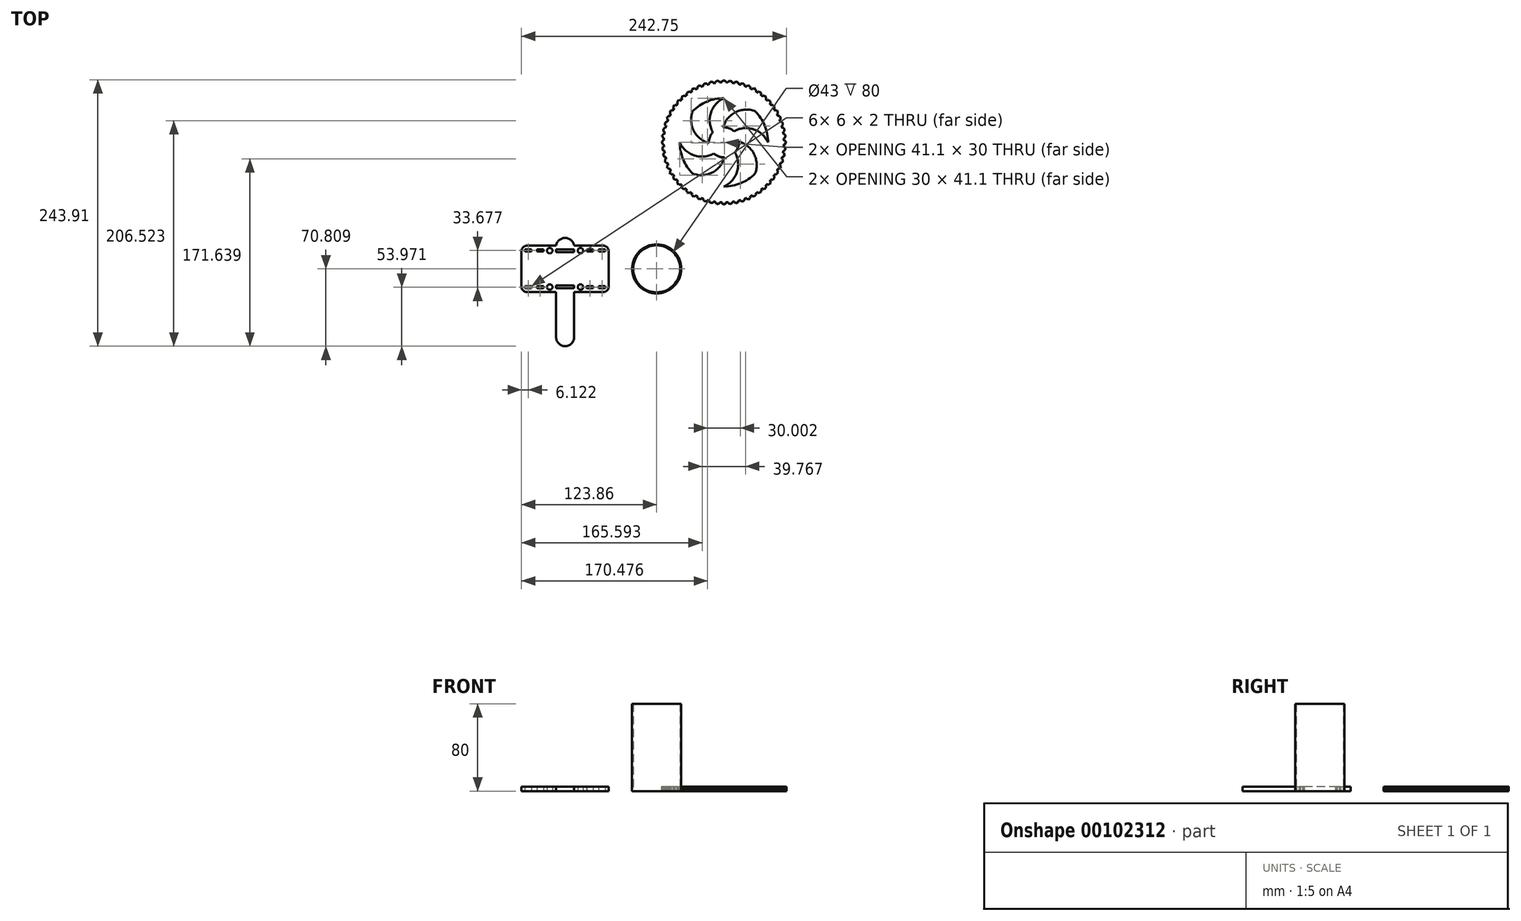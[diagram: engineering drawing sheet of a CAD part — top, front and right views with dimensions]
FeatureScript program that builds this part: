
annotation { "Feature Type Name" : "Feature", "Feature Type Description" : "" }
export const myFeature = defineFeature(function(context is Context, id is Id, definition is map)
    precondition{}
    {
        {
            var Q0;
            Q0=qCreatedBy(makeId("Top.planeOp"),FACE);
            var sketch = newSketch(context, id + "F0", { "sketchPlane" : qUnion([Q0])});
            skCircle(sketch, "E0", {"center": v(105.48, 9.3) * mm, "radius": 55 * mm});
            skLineSegment(sketch, "E1.bottom", {"start": v(-5, -85.33) * mm, "end": v(-31.7, -85.33) * mm});
            skLineSegment(sketch, "E1.top", {"start": v(-5, -127.71) * mm, "end": v(-31.7, -127.71) * mm});
            skLineSegment(sketch, "E1.left", {"start": v(0, -90.33) * mm, "end": v(0, -122.71) * mm});
            skLineSegment(sketch, "E1.right", {"start": v(-80, -90.33) * mm, "end": v(-80, -122.71) * mm});
            skArc(sketch, "E2", {"start": v(65.04, 9.3) * mm, "mid": v(68.12, -6.16) * mm, "end": v(76.89, -19.28) * mm});
            skArc(sketch, "E3", {"start": v(115.62, 0.11) * mm, "mid": v(118.37, 4.7) * mm, "end": v(119.15, 9.98) * mm});
            skArc(sketch, "E4", {"start": v(105.48, 49.74) * mm, "mid": v(93.48, 36.37) * mm, "end": v(95.33, 18.5) * mm});
            skArc(sketch, "E5.1.0", {"start": v(76.89, 37.9) * mm, "mid": v(77.86, 19.97) * mm, "end": v(91.8, 8.64) * mm});
            skArc(sketch, "E5.2.0", {"start": v(65.04, 9.3) * mm, "mid": v(78.41, -2.68) * mm, "end": v(96.28, -0.83) * mm});
            skArc(sketch, "E5.3.0", {"start": v(76.89, -19.28) * mm, "mid": v(94.82, -18.3) * mm, "end": v(106.14, -4.37) * mm});
            skArc(sketch, "E5.4.0", {"start": v(105.48, -31.13) * mm, "mid": v(117.47, -17.75) * mm, "end": v(115.62, 0.11) * mm});
            skArc(sketch, "E5.5.0", {"start": v(134.07, -19.28) * mm, "mid": v(133.1, -1.35) * mm, "end": v(119.15, 9.98) * mm});
            skArc(sketch, "E5.6.0", {"start": v(145.91, 9.3) * mm, "mid": v(132.54, 21.3) * mm, "end": v(114.68, 19.45) * mm});
            skArc(sketch, "E5.7.0", {"start": v(134.07, 37.9) * mm, "mid": v(116.13, 36.93) * mm, "end": v(104.8, 22.99) * mm});
            skArc(sketch, "E6.trimOffspring", {"start": v(95.33, 18.5) * mm, "mid": v(92.59, 13.93) * mm, "end": v(91.8, 8.64) * mm});
            skArc(sketch, "E7.trimOffspring", {"start": v(96.28, -0.83) * mm, "mid": v(100.86, -3.58) * mm, "end": v(106.14, -4.37) * mm});
            skArc(sketch, "E8.trimOffspring", {"start": v(105.48, -31.13) * mm, "mid": v(120.95, -28.05) * mm, "end": v(134.07, -19.28) * mm});
            skArc(sketch, "E9.trimOffspring", {"start": v(145.91, 9.3) * mm, "mid": v(142.83, 24.78) * mm, "end": v(134.07, 37.9) * mm});
            skArc(sketch, "E10.trimOffspring", {"start": v(105.48, 49.74) * mm, "mid": v(90, 46.67) * mm, "end": v(76.89, 37.9) * mm});
            skArc(sketch, "E11.trimOffspring", {"start": v(114.68, 19.45) * mm, "mid": v(110.1, 22.2) * mm, "end": v(104.8, 22.99) * mm});
            skLineSegment(sketch, "E12.bottom", {"start": v(-76.88, -124.36) * mm, "end": v(-70.88, -124.36) * mm});
            skLineSegment(sketch, "E12.top", {"start": v(-76.88, -122.36) * mm, "end": v(-70.88, -122.36) * mm});
            skLineSegment(sketch, "E12.left", {"start": v(-76.88, -124.36) * mm, "end": v(-76.88, -122.36) * mm});
            skLineSegment(sketch, "E12.right", {"start": v(-70.88, -124.36) * mm, "end": v(-70.88, -122.36) * mm});
            skLineSegment(sketch, "E13.bottom", {"start": v(-65.79, -124.36) * mm, "end": v(-59.79, -124.36) * mm});
            skLineSegment(sketch, "E13.top", {"start": v(-65.79, -122.36) * mm, "end": v(-59.79, -122.36) * mm});
            skLineSegment(sketch, "E13.left", {"start": v(-65.79, -124.36) * mm, "end": v(-65.79, -122.36) * mm});
            skLineSegment(sketch, "E13.right", {"start": v(-59.79, -124.36) * mm, "end": v(-59.79, -122.36) * mm});
            skLineSegment(sketch, "E14.MirrorCS", {"start": v(-76.88, -88.68) * mm, "end": v(-70.88, -88.68) * mm});
            skLineSegment(sketch, "E15.MirrorCS", {"start": v(-76.88, -88.68) * mm, "end": v(-76.88, -90.68) * mm});
            skLineSegment(sketch, "E16.MirrorCS", {"start": v(-70.88, -88.68) * mm, "end": v(-70.88, -90.68) * mm});
            skLineSegment(sketch, "E17.MirrorCS", {"start": v(-65.79, -88.68) * mm, "end": v(-65.79, -90.68) * mm});
            skLineSegment(sketch, "E18.MirrorCS", {"start": v(-65.79, -88.68) * mm, "end": v(-59.79, -88.68) * mm});
            skLineSegment(sketch, "E19.MirrorCS", {"start": v(-65.79, -90.68) * mm, "end": v(-59.79, -90.68) * mm});
            skLineSegment(sketch, "E20.MirrorCS", {"start": v(-59.87, -88.68) * mm, "end": v(-59.87, -90.68) * mm});
            skLineSegment(sketch, "E21", {"start": v(-76.88, -90.68) * mm, "end": v(-70.88, -90.68) * mm});
            skPoint(sketch, "E22.visualSharp", {"position": v(-80, -127.71) * mm});
            skArc(sketch, "E22.filletArc", {"start": v(-80, -122.71) * mm, "mid": v(-78.54, -126.25) * mm, "end": v(-75, -127.71) * mm});
            skPoint(sketch, "E23.visualSharp", {"position": v(0, -85.33) * mm});
            skArc(sketch, "E23.filletArc", {"start": v(0, -90.33) * mm, "mid": v(-1.46, -86.8) * mm, "end": v(-5, -85.33) * mm});
            skPoint(sketch, "E24.visualSharp", {"position": v(-80, -85.33) * mm});
            skArc(sketch, "E24.filletArc", {"start": v(-75, -85.33) * mm, "mid": v(-78.54, -86.8) * mm, "end": v(-80, -90.33) * mm});
            skLineSegment(sketch, "E25", {"start": v(-40, -127.71) * mm, "end": v(-40, -85.33) * mm, "construction": true});
            skLineSegment(sketch, "E26.MirrorCS", {"start": v(-14.21, -124.36) * mm, "end": v(-14.21, -122.36) * mm});
            skLineSegment(sketch, "E27.MirrorCS", {"start": v(-9.12, -124.36) * mm, "end": v(-9.12, -122.36) * mm});
            skLineSegment(sketch, "E28.MirrorCS", {"start": v(-9.12, -88.68) * mm, "end": v(-9.12, -90.68) * mm});
            skLineSegment(sketch, "E29.MirrorCS", {"start": v(-3.12, -88.68) * mm, "end": v(-3.12, -90.68) * mm});
            skLineSegment(sketch, "E30.MirrorCS", {"start": v(-3.12, -88.68) * mm, "end": v(-9.12, -88.68) * mm});
            skLineSegment(sketch, "E31.MirrorCS", {"start": v(-20.13, -88.68) * mm, "end": v(-20.13, -90.68) * mm});
            skLineSegment(sketch, "E32.MirrorCS", {"start": v(-14.21, -88.68) * mm, "end": v(-14.21, -90.68) * mm});
            skLineSegment(sketch, "E33.MirrorCS", {"start": v(-3.12, -124.36) * mm, "end": v(-9.12, -124.36) * mm});
            skLineSegment(sketch, "E34.MirrorCS", {"start": v(-3.12, -124.36) * mm, "end": v(-3.12, -122.36) * mm});
            skLineSegment(sketch, "E35.MirrorCS", {"start": v(-20.21, -124.36) * mm, "end": v(-20.21, -122.36) * mm});
            skLineSegment(sketch, "E36.MirrorCS", {"start": v(-3.12, -122.36) * mm, "end": v(-9.12, -122.36) * mm});
            skLineSegment(sketch, "E37.MirrorCS", {"start": v(-3.12, -90.68) * mm, "end": v(-9.12, -90.68) * mm});
            skPoint(sketch, "E38.MirrorP", {"position": v(0, -127.71) * mm});
            skLineSegment(sketch, "E39.MirrorCS", {"start": v(-14.21, -122.36) * mm, "end": v(-20.21, -122.36) * mm});
            skLineSegment(sketch, "E40.MirrorCS", {"start": v(-14.21, -124.36) * mm, "end": v(-20.21, -124.36) * mm});
            skLineSegment(sketch, "E41.MirrorCS", {"start": v(-14.21, -90.68) * mm, "end": v(-20.21, -90.68) * mm});
            skLineSegment(sketch, "E42.MirrorCS", {"start": v(-14.21, -88.68) * mm, "end": v(-20.21, -88.68) * mm});
            skArc(sketch, "E43.MirrorCS", {"start": v(0, -122.71) * mm, "mid": v(-1.46, -126.25) * mm, "end": v(-5, -127.71) * mm});
            skLineSegment(sketch, "E44.bottom", {"start": v(-48.3, -124.25) * mm, "end": v(-31.7, -124.25) * mm});
            skLineSegment(sketch, "E44.top", {"start": v(-48.3, -121.77) * mm, "end": v(-31.7, -121.77) * mm});
            skLineSegment(sketch, "E44.left", {"start": v(-48.3, -124.25) * mm, "end": v(-48.3, -121.77) * mm});
            skLineSegment(sketch, "E44.right", {"start": v(-31.7, -124.25) * mm, "end": v(-31.7, -121.77) * mm});
            skPoint(sketch, "E44.middle", {"position": v(-40, -123) * mm});
            skLineSegment(sketch, "E45", {"start": v(-40, -106.52) * mm, "end": v(-20.74, -106.52) * mm, "construction": true});
            skLineSegment(sketch, "E46.MirrorCS", {"start": v(-48.3, -91.28) * mm, "end": v(-31.7, -91.28) * mm});
            skLineSegment(sketch, "E47.MirrorCS", {"start": v(-48.3, -88.79) * mm, "end": v(-48.3, -91.28) * mm});
            skLineSegment(sketch, "E48.MirrorCS", {"start": v(-48.3, -88.79) * mm, "end": v(-31.7, -88.79) * mm});
            skLineSegment(sketch, "E49.MirrorCS", {"start": v(-31.7, -88.79) * mm, "end": v(-31.7, -91.28) * mm});
            skLineSegment(sketch, "E50", {"start": v(-59.87, -89.68) * mm, "end": v(-48.3, -90.03) * mm, "construction": true});
            skCircle(sketch, "E51", {"center": v(-54.09, -89.86) * mm, "radius": 2.5 * mm});
            skCircle(sketch, "E52.MirrorC", {"center": v(-25.91, -89.86) * mm, "radius": 2.5 * mm});
            skCircle(sketch, "E53.MirrorC", {"center": v(-25.91, -123.18) * mm, "radius": 2.5 * mm});
            skCircle(sketch, "E54.MirrorC", {"center": v(-54.09, -123.18) * mm, "radius": 2.5 * mm});
            skCircle(sketch, "E55", {"center": v(43.86, -106.52) * mm, "radius": 21.5 * mm});
            skPoint(sketch, "E55.centerSnap0", {"position": v(0, -106.52) * mm});
            skCircle(sketch, "E56.0", {"center": v(43.86, -106.52) * mm, "radius": 22.5 * mm});
            skArc(sketch, "E57.MirrorCS", {"start": v(-48.3, -85.33) * mm, "mid": v(-40, -78.22) * mm, "end": v(-31.7, -85.33) * mm});
            skLineSegment(sketch, "E58", {"start": v(-48.3, -127.71) * mm, "end": v(-48.3, -169.03) * mm});
            skLineSegment(sketch, "E59", {"start": v(-31.7, -127.71) * mm, "end": v(-31.7, -169.03) * mm});
            skArc(sketch, "E60", {"start": v(-48.3, -169.03) * mm, "mid": v(-40, -177.33) * mm, "end": v(-31.7, -169.03) * mm});
            skLineSegment(sketch, "E61.trimOffspring", {"start": v(-48.3, -127.71) * mm, "end": v(-75, -127.71) * mm});
            skLineSegment(sketch, "E62.trimOffspring", {"start": v(-48.3, -85.33) * mm, "end": v(-75, -85.33) * mm});
            skLineSegment(sketch, "E63", {"start": v(105.48, 9.3) * mm, "end": v(105.48, -47.96) * mm, "construction": true});
            skArc(sketch, "E64", {"start": v(106.51, -47) * mm, "mid": v(105.78, -47.26) * mm, "end": v(105.48, -47.96) * mm});
            skArc(sketch, "E65", {"start": v(106.51, -47) * mm, "mid": v(107.3, -46.57) * mm, "end": v(107.26, -45.66) * mm});
            skArc(sketch, "E66.MirrorCS", {"start": v(104.44, -47) * mm, "mid": v(103.65, -46.57) * mm, "end": v(103.7, -45.66) * mm});
            skArc(sketch, "E67.MirrorCS", {"start": v(104.44, -47) * mm, "mid": v(105.17, -47.26) * mm, "end": v(105.48, -47.96) * mm});
            skArc(sketch, "E68.1.0", {"start": v(112.4, -46.59) * mm, "mid": v(111.7, -46.91) * mm, "end": v(111.46, -47.65) * mm});
            skArc(sketch, "E68.1.1", {"start": v(110.33, -46.8) * mm, "mid": v(109.5, -46.45) * mm, "end": v(109.45, -45.55) * mm});
            skArc(sketch, "E68.1.2", {"start": v(110.33, -46.8) * mm, "mid": v(111.08, -46.98) * mm, "end": v(111.46, -47.65) * mm});
            skArc(sketch, "E68.1.3", {"start": v(112.4, -46.59) * mm, "mid": v(113.14, -46.07) * mm, "end": v(113, -45.17) * mm});
            skArc(sketch, "E68.2.0", {"start": v(118.2, -45.56) * mm, "mid": v(117.54, -45.96) * mm, "end": v(117.38, -46.71) * mm});
            skArc(sketch, "E68.2.1", {"start": v(116.17, -45.99) * mm, "mid": v(115.3, -45.73) * mm, "end": v(115.17, -44.83) * mm});
            skArc(sketch, "E68.2.2", {"start": v(116.17, -45.99) * mm, "mid": v(116.94, -46.08) * mm, "end": v(117.38, -46.71) * mm});
            skArc(sketch, "E68.2.3", {"start": v(118.2, -45.56) * mm, "mid": v(118.89, -44.97) * mm, "end": v(118.65, -44.1) * mm});
            skArc(sketch, "E68.3.0", {"start": v(123.86, -43.93) * mm, "mid": v(123.25, -44.4) * mm, "end": v(123.17, -45.16) * mm});
            skArc(sketch, "E68.3.1", {"start": v(121.9, -44.57) * mm, "mid": v(121, -44.4) * mm, "end": v(120.77, -43.52) * mm});
            skArc(sketch, "E68.3.2", {"start": v(121.9, -44.57) * mm, "mid": v(122.66, -44.58) * mm, "end": v(123.17, -45.16) * mm});
            skArc(sketch, "E68.3.3", {"start": v(123.86, -43.93) * mm, "mid": v(124.49, -43.27) * mm, "end": v(124.16, -42.42) * mm});
            skArc(sketch, "E68.4.0", {"start": v(129.33, -41.71) * mm, "mid": v(128.77, -42.24) * mm, "end": v(128.77, -43.01) * mm});
            skArc(sketch, "E68.4.1", {"start": v(127.44, -42.56) * mm, "mid": v(126.53, -42.48) * mm, "end": v(126.2, -41.63) * mm});
            skArc(sketch, "E68.4.2", {"start": v(127.44, -42.56) * mm, "mid": v(128.2, -42.5) * mm, "end": v(128.77, -43.01) * mm});
            skArc(sketch, "E68.4.3", {"start": v(129.33, -41.71) * mm, "mid": v(129.88, -41) * mm, "end": v(129.46, -40.19) * mm});
            skArc(sketch, "E68.5.0", {"start": v(134.53, -38.94) * mm, "mid": v(134.03, -39.52) * mm, "end": v(134.11, -40.29) * mm});
            skArc(sketch, "E68.5.1", {"start": v(132.74, -39.98) * mm, "mid": v(131.83, -40) * mm, "end": v(131.42, -39.19) * mm});
            skArc(sketch, "E68.5.2", {"start": v(132.74, -39.98) * mm, "mid": v(133.5, -39.83) * mm, "end": v(134.11, -40.29) * mm});
            skArc(sketch, "E68.5.3", {"start": v(134.53, -38.94) * mm, "mid": v(135, -38.17) * mm, "end": v(134.5, -37.4) * mm});
            skArc(sketch, "E68.6.0", {"start": v(139.41, -35.64) * mm, "mid": v(138.97, -36.27) * mm, "end": v(139.14, -37.02) * mm});
            skArc(sketch, "E68.6.1", {"start": v(137.74, -36.86) * mm, "mid": v(136.84, -36.97) * mm, "end": v(136.35, -36.2) * mm});
            skArc(sketch, "E68.6.2", {"start": v(137.74, -36.86) * mm, "mid": v(138.48, -36.63) * mm, "end": v(139.14, -37.02) * mm});
            skArc(sketch, "E68.6.3", {"start": v(139.41, -35.64) * mm, "mid": v(139.8, -34.82) * mm, "end": v(139.23, -34.12) * mm});
            skArc(sketch, "E68.7.0", {"start": v(143.93, -31.85) * mm, "mid": v(143.56, -32.52) * mm, "end": v(143.8, -33.25) * mm});
            skArc(sketch, "E68.7.1", {"start": v(142.39, -33.23) * mm, "mid": v(141.5, -33.44) * mm, "end": v(140.94, -32.73) * mm});
            skArc(sketch, "E68.7.2", {"start": v(142.39, -33.23) * mm, "mid": v(143.1, -32.93) * mm, "end": v(143.8, -33.25) * mm});
            skArc(sketch, "E68.7.3", {"start": v(143.93, -31.85) * mm, "mid": v(144.23, -30.99) * mm, "end": v(143.58, -30.35) * mm});
            skArc(sketch, "E68.8.0", {"start": v(148.02, -27.6) * mm, "mid": v(147.72, -28.31) * mm, "end": v(148.04, -29.01) * mm});
            skArc(sketch, "E68.8.1", {"start": v(146.63, -29.14) * mm, "mid": v(145.78, -29.44) * mm, "end": v(145.14, -28.8) * mm});
            skArc(sketch, "E68.8.2", {"start": v(146.63, -29.14) * mm, "mid": v(147.3, -28.77) * mm, "end": v(148.04, -29.01) * mm});
            skArc(sketch, "E68.8.3", {"start": v(148.02, -27.6) * mm, "mid": v(148.23, -26.72) * mm, "end": v(147.52, -26.15) * mm});
            skArc(sketch, "E68.9.0", {"start": v(151.64, -22.95) * mm, "mid": v(151.42, -23.69) * mm, "end": v(151.81, -24.35) * mm});
            skArc(sketch, "E68.9.1", {"start": v(150.43, -24.63) * mm, "mid": v(149.6, -25.02) * mm, "end": v(148.9, -24.44) * mm});
            skArc(sketch, "E68.9.2", {"start": v(150.43, -24.63) * mm, "mid": v(151.06, -24.19) * mm, "end": v(151.81, -24.35) * mm});
            skArc(sketch, "E68.9.3", {"start": v(151.64, -22.95) * mm, "mid": v(151.76, -22.05) * mm, "end": v(151, -21.56) * mm});
            skArc(sketch, "E68.10.0", {"start": v(154.76, -17.95) * mm, "mid": v(154.62, -18.7) * mm, "end": v(155.08, -19.33) * mm});
            skArc(sketch, "E68.10.1", {"start": v(153.73, -19.74) * mm, "mid": v(152.95, -20.22) * mm, "end": v(152.2, -19.72) * mm});
            skArc(sketch, "E68.10.2", {"start": v(153.73, -19.74) * mm, "mid": v(154.31, -19.24) * mm, "end": v(155.08, -19.33) * mm});
            skArc(sketch, "E68.10.3", {"start": v(154.76, -17.95) * mm, "mid": v(154.78, -17.04) * mm, "end": v(153.97, -16.64) * mm});
            skArc(sketch, "E68.11.0", {"start": v(157.34, -12.65) * mm, "mid": v(157.28, -13.42) * mm, "end": v(157.8, -13.98) * mm});
            skArc(sketch, "E68.11.1", {"start": v(156.5, -14.54) * mm, "mid": v(155.78, -15.1) * mm, "end": v(154.97, -14.67) * mm});
            skArc(sketch, "E68.11.2", {"start": v(156.5, -14.54) * mm, "mid": v(157.03, -13.98) * mm, "end": v(157.8, -13.98) * mm});
            skArc(sketch, "E68.11.3", {"start": v(157.34, -12.65) * mm, "mid": v(157.27, -11.74) * mm, "end": v(156.42, -11.42) * mm});
            skArc(sketch, "E68.12.0", {"start": v(159.35, -7.1) * mm, "mid": v(159.37, -7.88) * mm, "end": v(159.95, -8.39) * mm});
            skArc(sketch, "E68.12.1", {"start": v(158.71, -9.08) * mm, "mid": v(158.05, -9.7) * mm, "end": v(157.2, -9.37) * mm});
            skArc(sketch, "E68.12.2", {"start": v(158.71, -9.08) * mm, "mid": v(159.18, -8.46) * mm, "end": v(159.95, -8.39) * mm});
            skArc(sketch, "E68.12.3", {"start": v(159.35, -7.1) * mm, "mid": v(159.18, -6.22) * mm, "end": v(158.3, -5.99) * mm});
            skArc(sketch, "E68.13.0", {"start": v(160.77, -1.39) * mm, "mid": v(160.87, -2.15) * mm, "end": v(161.5, -2.6) * mm});
            skArc(sketch, "E68.13.1", {"start": v(160.34, -3.41) * mm, "mid": v(159.75, -4.1) * mm, "end": v(158.88, -3.86) * mm});
            skArc(sketch, "E68.13.2", {"start": v(160.34, -3.41) * mm, "mid": v(160.74, -2.75) * mm, "end": v(161.5, -2.6) * mm});
            skArc(sketch, "E68.13.3", {"start": v(160.77, -1.39) * mm, "mid": v(160.51, -0.52) * mm, "end": v(159.62, -0.38) * mm});
            skArc(sketch, "E68.14.0", {"start": v(161.59, 4.45) * mm, "mid": v(161.76, 3.7) * mm, "end": v(162.43, 3.32) * mm});
            skArc(sketch, "E68.14.1", {"start": v(161.37, 2.4) * mm, "mid": v(160.86, 1.65) * mm, "end": v(159.96, 1.8) * mm});
            skArc(sketch, "E68.14.2", {"start": v(161.37, 2.4) * mm, "mid": v(161.7, 3.1) * mm, "end": v(162.43, 3.32) * mm});
            skArc(sketch, "E68.14.3", {"start": v(161.59, 4.45) * mm, "mid": v(161.24, 5.3) * mm, "end": v(160.33, 5.33) * mm});
            skArc(sketch, "E68.15.0", {"start": v(161.79, 10.34) * mm, "mid": v(162.04, 9.62) * mm, "end": v(162.75, 9.3) * mm});
            skArc(sketch, "E68.15.1", {"start": v(161.79, 8.27) * mm, "mid": v(161.35, 7.48) * mm, "end": v(160.45, 7.53) * mm});
            skArc(sketch, "E68.15.2", {"start": v(161.79, 8.27) * mm, "mid": v(162.04, 9) * mm, "end": v(162.75, 9.3) * mm});
            skArc(sketch, "E68.15.3", {"start": v(161.79, 10.34) * mm, "mid": v(161.35, 11.14) * mm, "end": v(160.45, 11.09) * mm});
            skArc(sketch, "E68.16.0", {"start": v(161.37, 16.23) * mm, "mid": v(161.7, 15.53) * mm, "end": v(162.43, 15.3) * mm});
            skArc(sketch, "E68.16.1", {"start": v(161.59, 14.17) * mm, "mid": v(161.24, 13.33) * mm, "end": v(160.33, 13.29) * mm});
            skArc(sketch, "E68.16.2", {"start": v(161.59, 14.17) * mm, "mid": v(161.76, 14.92) * mm, "end": v(162.43, 15.3) * mm});
            skArc(sketch, "E68.16.3", {"start": v(161.37, 16.23) * mm, "mid": v(160.86, 16.97) * mm, "end": v(159.96, 16.83) * mm});
            skArc(sketch, "E68.17.0", {"start": v(160.34, 22.03) * mm, "mid": v(160.74, 21.37) * mm, "end": v(161.5, 21.22) * mm});
            skArc(sketch, "E68.17.1", {"start": v(160.77, 20) * mm, "mid": v(160.51, 19.14) * mm, "end": v(159.62, 19) * mm});
            skArc(sketch, "E68.17.2", {"start": v(160.77, 20) * mm, "mid": v(160.87, 20.77) * mm, "end": v(161.5, 21.22) * mm});
            skArc(sketch, "E68.17.3", {"start": v(160.34, 22.03) * mm, "mid": v(159.75, 22.72) * mm, "end": v(158.88, 22.48) * mm});
            skArc(sketch, "E68.18.0", {"start": v(158.71, 27.7) * mm, "mid": v(159.18, 27.08) * mm, "end": v(159.95, 27) * mm});
            skArc(sketch, "E68.18.1", {"start": v(159.35, 25.73) * mm, "mid": v(159.18, 24.83) * mm, "end": v(158.3, 24.6) * mm});
            skArc(sketch, "E68.18.2", {"start": v(159.35, 25.73) * mm, "mid": v(159.37, 26.5) * mm, "end": v(159.95, 27) * mm});
            skArc(sketch, "E68.18.3", {"start": v(158.71, 27.7) * mm, "mid": v(158.05, 28.32) * mm, "end": v(157.2, 27.99) * mm});
            skArc(sketch, "E68.19.0", {"start": v(156.5, 33.16) * mm, "mid": v(157.03, 32.6) * mm, "end": v(157.8, 32.6) * mm});
            skArc(sketch, "E68.19.1", {"start": v(157.34, 31.27) * mm, "mid": v(157.27, 30.36) * mm, "end": v(156.42, 30.04) * mm});
            skArc(sketch, "E68.19.2", {"start": v(157.34, 31.27) * mm, "mid": v(157.28, 32.04) * mm, "end": v(157.8, 32.6) * mm});
            skArc(sketch, "E68.19.3", {"start": v(156.5, 33.16) * mm, "mid": v(155.78, 33.7) * mm, "end": v(154.97, 33.3) * mm});
            skArc(sketch, "E68.20.0", {"start": v(153.73, 38.36) * mm, "mid": v(154.31, 37.86) * mm, "end": v(155.08, 37.95) * mm});
            skArc(sketch, "E68.20.1", {"start": v(154.76, 36.57) * mm, "mid": v(154.78, 35.66) * mm, "end": v(153.97, 35.25) * mm});
            skArc(sketch, "E68.20.2", {"start": v(154.76, 36.57) * mm, "mid": v(154.62, 37.33) * mm, "end": v(155.08, 37.95) * mm});
            skArc(sketch, "E68.20.3", {"start": v(153.73, 38.36) * mm, "mid": v(152.95, 38.83) * mm, "end": v(152.2, 38.34) * mm});
            skArc(sketch, "E68.21.0", {"start": v(150.43, 43.25) * mm, "mid": v(151.06, 42.8) * mm, "end": v(151.81, 42.97) * mm});
            skArc(sketch, "E68.21.1", {"start": v(151.64, 41.57) * mm, "mid": v(151.76, 40.67) * mm, "end": v(151, 40.18) * mm});
            skArc(sketch, "E68.21.2", {"start": v(151.64, 41.57) * mm, "mid": v(151.42, 42.3) * mm, "end": v(151.81, 42.97) * mm});
            skArc(sketch, "E68.21.3", {"start": v(150.43, 43.25) * mm, "mid": v(149.6, 43.63) * mm, "end": v(148.9, 43.06) * mm});
            skArc(sketch, "E68.22.0", {"start": v(146.63, 47.76) * mm, "mid": v(147.3, 47.39) * mm, "end": v(148.04, 47.63) * mm});
            skArc(sketch, "E68.22.1", {"start": v(148.02, 46.22) * mm, "mid": v(148.23, 45.34) * mm, "end": v(147.52, 44.77) * mm});
            skArc(sketch, "E68.22.2", {"start": v(148.02, 46.22) * mm, "mid": v(147.72, 46.93) * mm, "end": v(148.04, 47.63) * mm});
            skArc(sketch, "E68.22.3", {"start": v(146.63, 47.76) * mm, "mid": v(145.78, 48.06) * mm, "end": v(145.14, 47.41) * mm});
            skArc(sketch, "E68.23.0", {"start": v(142.39, 51.85) * mm, "mid": v(143.1, 51.55) * mm, "end": v(143.8, 51.87) * mm});
            skArc(sketch, "E68.23.1", {"start": v(143.93, 50.47) * mm, "mid": v(144.23, 49.6) * mm, "end": v(143.58, 48.97) * mm});
            skArc(sketch, "E68.23.2", {"start": v(143.93, 50.47) * mm, "mid": v(143.56, 51.14) * mm, "end": v(143.8, 51.87) * mm});
            skArc(sketch, "E68.23.3", {"start": v(142.39, 51.85) * mm, "mid": v(141.5, 52.06) * mm, "end": v(140.94, 51.35) * mm});
            skArc(sketch, "E68.24.0", {"start": v(137.74, 55.48) * mm, "mid": v(138.48, 55.25) * mm, "end": v(139.14, 55.64) * mm});
            skArc(sketch, "E68.24.1", {"start": v(139.41, 54.26) * mm, "mid": v(139.8, 53.44) * mm, "end": v(139.23, 52.74) * mm});
            skArc(sketch, "E68.24.2", {"start": v(139.41, 54.26) * mm, "mid": v(138.97, 54.9) * mm, "end": v(139.14, 55.64) * mm});
            skArc(sketch, "E68.24.3", {"start": v(137.74, 55.48) * mm, "mid": v(136.84, 55.6) * mm, "end": v(136.35, 54.83) * mm});
            skArc(sketch, "E68.25.0", {"start": v(132.74, 58.6) * mm, "mid": v(133.5, 58.45) * mm, "end": v(134.11, 58.9) * mm});
            skArc(sketch, "E68.25.1", {"start": v(134.53, 57.56) * mm, "mid": v(135, 56.78) * mm, "end": v(134.5, 56.03) * mm});
            skArc(sketch, "E68.25.2", {"start": v(134.53, 57.56) * mm, "mid": v(134.03, 58.14) * mm, "end": v(134.11, 58.9) * mm});
            skArc(sketch, "E68.25.3", {"start": v(132.74, 58.6) * mm, "mid": v(131.83, 58.62) * mm, "end": v(131.42, 57.8) * mm});
            skArc(sketch, "E68.26.0", {"start": v(127.44, 61.17) * mm, "mid": v(128.2, 61.11) * mm, "end": v(128.77, 61.63) * mm});
            skArc(sketch, "E68.26.1", {"start": v(129.33, 60.33) * mm, "mid": v(129.88, 59.61) * mm, "end": v(129.46, 58.8) * mm});
            skArc(sketch, "E68.26.2", {"start": v(129.33, 60.33) * mm, "mid": v(128.77, 60.86) * mm, "end": v(128.77, 61.63) * mm});
            skArc(sketch, "E68.26.3", {"start": v(127.44, 61.17) * mm, "mid": v(126.53, 61.1) * mm, "end": v(126.2, 60.25) * mm});
            skArc(sketch, "E68.27.0", {"start": v(121.9, 63.19) * mm, "mid": v(122.66, 63.2) * mm, "end": v(123.17, 63.78) * mm});
            skArc(sketch, "E68.27.1", {"start": v(123.86, 62.55) * mm, "mid": v(124.49, 61.89) * mm, "end": v(124.16, 61.04) * mm});
            skArc(sketch, "E68.27.2", {"start": v(123.86, 62.55) * mm, "mid": v(123.25, 63.01) * mm, "end": v(123.17, 63.78) * mm});
            skArc(sketch, "E68.27.3", {"start": v(121.9, 63.19) * mm, "mid": v(121, 63.02) * mm, "end": v(120.77, 62.14) * mm});
            skArc(sketch, "E68.28.0", {"start": v(116.17, 64.6) * mm, "mid": v(116.94, 64.7) * mm, "end": v(117.38, 65.33) * mm});
            skArc(sketch, "E68.28.1", {"start": v(118.2, 64.18) * mm, "mid": v(118.89, 63.58) * mm, "end": v(118.65, 62.7) * mm});
            skArc(sketch, "E68.28.2", {"start": v(118.2, 64.18) * mm, "mid": v(117.54, 64.58) * mm, "end": v(117.38, 65.33) * mm});
            skArc(sketch, "E68.28.3", {"start": v(116.17, 64.6) * mm, "mid": v(115.3, 64.35) * mm, "end": v(115.17, 63.45) * mm});
            skArc(sketch, "E68.29.0", {"start": v(110.33, 65.42) * mm, "mid": v(111.08, 65.6) * mm, "end": v(111.46, 66.27) * mm});
            skArc(sketch, "E68.29.1", {"start": v(112.4, 65.2) * mm, "mid": v(113.14, 64.69) * mm, "end": v(113, 63.8) * mm});
            skArc(sketch, "E68.29.2", {"start": v(112.4, 65.2) * mm, "mid": v(111.7, 65.53) * mm, "end": v(111.46, 66.27) * mm});
            skArc(sketch, "E68.29.3", {"start": v(110.33, 65.42) * mm, "mid": v(109.5, 65.07) * mm, "end": v(109.45, 64.17) * mm});
            skArc(sketch, "E68.30.0", {"start": v(104.44, 65.62) * mm, "mid": v(105.17, 65.88) * mm, "end": v(105.48, 66.58) * mm});
            skArc(sketch, "E68.30.1", {"start": v(106.51, 65.62) * mm, "mid": v(107.3, 65.19) * mm, "end": v(107.26, 64.28) * mm});
            skArc(sketch, "E68.30.2", {"start": v(106.51, 65.62) * mm, "mid": v(105.78, 65.88) * mm, "end": v(105.48, 66.58) * mm});
            skArc(sketch, "E68.30.3", {"start": v(104.44, 65.62) * mm, "mid": v(103.65, 65.19) * mm, "end": v(103.7, 64.28) * mm});
            skArc(sketch, "E68.31.0", {"start": v(98.56, 65.2) * mm, "mid": v(99.26, 65.53) * mm, "end": v(99.5, 66.27) * mm});
            skArc(sketch, "E68.31.1", {"start": v(100.62, 65.42) * mm, "mid": v(101.46, 65.07) * mm, "end": v(101.5, 64.17) * mm});
            skArc(sketch, "E68.31.2", {"start": v(100.62, 65.42) * mm, "mid": v(99.87, 65.6) * mm, "end": v(99.5, 66.27) * mm});
            skArc(sketch, "E68.31.3", {"start": v(98.56, 65.2) * mm, "mid": v(97.81, 64.69) * mm, "end": v(97.96, 63.8) * mm});
            skArc(sketch, "E68.32.0", {"start": v(92.76, 64.18) * mm, "mid": v(93.41, 64.58) * mm, "end": v(93.57, 65.33) * mm});
            skArc(sketch, "E68.32.1", {"start": v(94.78, 64.6) * mm, "mid": v(95.65, 64.35) * mm, "end": v(95.79, 63.45) * mm});
            skArc(sketch, "E68.32.2", {"start": v(94.78, 64.6) * mm, "mid": v(94.02, 64.7) * mm, "end": v(93.57, 65.33) * mm});
            skArc(sketch, "E68.32.3", {"start": v(92.76, 64.18) * mm, "mid": v(92.07, 63.58) * mm, "end": v(92.3, 62.7) * mm});
            skArc(sketch, "E68.33.0", {"start": v(87.1, 62.55) * mm, "mid": v(87.7, 63.01) * mm, "end": v(87.78, 63.78) * mm});
            skArc(sketch, "E68.33.1", {"start": v(89.06, 63.19) * mm, "mid": v(89.95, 63.02) * mm, "end": v(90.18, 62.14) * mm});
            skArc(sketch, "E68.33.2", {"start": v(89.06, 63.19) * mm, "mid": v(88.29, 63.2) * mm, "end": v(87.78, 63.78) * mm});
            skArc(sketch, "E68.33.3", {"start": v(87.1, 62.55) * mm, "mid": v(86.47, 61.89) * mm, "end": v(86.8, 61.04) * mm});
            skArc(sketch, "E68.34.0", {"start": v(81.63, 60.33) * mm, "mid": v(82.19, 60.86) * mm, "end": v(82.18, 61.63) * mm});
            skArc(sketch, "E68.34.1", {"start": v(83.52, 61.17) * mm, "mid": v(84.42, 61.1) * mm, "end": v(84.74, 60.25) * mm});
            skArc(sketch, "E68.34.2", {"start": v(83.52, 61.17) * mm, "mid": v(82.75, 61.11) * mm, "end": v(82.18, 61.63) * mm});
            skArc(sketch, "E68.34.3", {"start": v(81.63, 60.33) * mm, "mid": v(81.08, 59.61) * mm, "end": v(81.5, 58.8) * mm});
            skArc(sketch, "E68.35.0", {"start": v(76.42, 57.56) * mm, "mid": v(76.93, 58.14) * mm, "end": v(76.84, 58.9) * mm});
            skArc(sketch, "E68.35.1", {"start": v(78.22, 58.6) * mm, "mid": v(79.12, 58.62) * mm, "end": v(79.53, 57.8) * mm});
            skArc(sketch, "E68.35.2", {"start": v(78.22, 58.6) * mm, "mid": v(77.46, 58.45) * mm, "end": v(76.84, 58.9) * mm});
            skArc(sketch, "E68.35.3", {"start": v(76.42, 57.56) * mm, "mid": v(75.95, 56.78) * mm, "end": v(76.45, 56.03) * mm});
            skArc(sketch, "E68.36.0", {"start": v(71.54, 54.26) * mm, "mid": v(71.98, 54.9) * mm, "end": v(71.81, 55.64) * mm});
            skArc(sketch, "E68.36.1", {"start": v(73.21, 55.48) * mm, "mid": v(74.11, 55.6) * mm, "end": v(74.6, 54.83) * mm});
            skArc(sketch, "E68.36.2", {"start": v(73.21, 55.48) * mm, "mid": v(72.48, 55.25) * mm, "end": v(71.81, 55.64) * mm});
            skArc(sketch, "E68.36.3", {"start": v(71.54, 54.26) * mm, "mid": v(71.15, 53.44) * mm, "end": v(71.73, 52.74) * mm});
            skArc(sketch, "E68.37.0", {"start": v(67.03, 50.47) * mm, "mid": v(67.4, 51.14) * mm, "end": v(67.15, 51.87) * mm});
            skArc(sketch, "E68.37.1", {"start": v(68.57, 51.85) * mm, "mid": v(69.45, 52.06) * mm, "end": v(70.02, 51.35) * mm});
            skArc(sketch, "E68.37.2", {"start": v(68.57, 51.85) * mm, "mid": v(67.86, 51.55) * mm, "end": v(67.15, 51.87) * mm});
            skArc(sketch, "E68.37.3", {"start": v(67.03, 50.47) * mm, "mid": v(66.73, 49.6) * mm, "end": v(67.37, 48.97) * mm});
            skArc(sketch, "E68.38.0", {"start": v(62.94, 46.22) * mm, "mid": v(63.23, 46.93) * mm, "end": v(62.92, 47.63) * mm});
            skArc(sketch, "E68.38.1", {"start": v(64.32, 47.76) * mm, "mid": v(65.18, 48.06) * mm, "end": v(65.82, 47.41) * mm});
            skArc(sketch, "E68.38.2", {"start": v(64.32, 47.76) * mm, "mid": v(63.65, 47.39) * mm, "end": v(62.92, 47.63) * mm});
            skArc(sketch, "E68.38.3", {"start": v(62.94, 46.22) * mm, "mid": v(62.73, 45.34) * mm, "end": v(63.43, 44.77) * mm});
            skArc(sketch, "E68.39.0", {"start": v(59.31, 41.57) * mm, "mid": v(59.53, 42.3) * mm, "end": v(59.14, 42.97) * mm});
            skArc(sketch, "E68.39.1", {"start": v(60.53, 43.25) * mm, "mid": v(61.35, 43.63) * mm, "end": v(62.05, 43.06) * mm});
            skArc(sketch, "E68.39.2", {"start": v(60.53, 43.25) * mm, "mid": v(59.9, 42.8) * mm, "end": v(59.14, 42.97) * mm});
            skArc(sketch, "E68.39.3", {"start": v(59.31, 41.57) * mm, "mid": v(59.2, 40.67) * mm, "end": v(59.96, 40.18) * mm});
            skArc(sketch, "E68.40.0", {"start": v(56.2, 36.57) * mm, "mid": v(56.34, 37.33) * mm, "end": v(55.88, 37.95) * mm});
            skArc(sketch, "E68.40.1", {"start": v(57.23, 38.36) * mm, "mid": v(58, 38.83) * mm, "end": v(58.76, 38.34) * mm});
            skArc(sketch, "E68.40.2", {"start": v(57.23, 38.36) * mm, "mid": v(56.64, 37.86) * mm, "end": v(55.88, 37.95) * mm});
            skArc(sketch, "E68.40.3", {"start": v(56.2, 36.57) * mm, "mid": v(56.17, 35.66) * mm, "end": v(56.98, 35.25) * mm});
            skArc(sketch, "E68.41.0", {"start": v(53.61, 31.27) * mm, "mid": v(53.68, 32.04) * mm, "end": v(53.16, 32.6) * mm});
            skArc(sketch, "E68.41.1", {"start": v(54.45, 33.16) * mm, "mid": v(55.18, 33.7) * mm, "end": v(55.98, 33.3) * mm});
            skArc(sketch, "E68.41.2", {"start": v(54.45, 33.16) * mm, "mid": v(53.93, 32.6) * mm, "end": v(53.16, 32.6) * mm});
            skArc(sketch, "E68.41.3", {"start": v(53.61, 31.27) * mm, "mid": v(53.69, 30.36) * mm, "end": v(54.53, 30.04) * mm});
            skArc(sketch, "E68.42.0", {"start": v(51.6, 25.73) * mm, "mid": v(51.58, 26.5) * mm, "end": v(51, 27) * mm});
            skArc(sketch, "E68.42.1", {"start": v(52.24, 27.7) * mm, "mid": v(52.9, 28.32) * mm, "end": v(53.75, 27.99) * mm});
            skArc(sketch, "E68.42.2", {"start": v(52.24, 27.7) * mm, "mid": v(51.77, 27.08) * mm, "end": v(51, 27) * mm});
            skArc(sketch, "E68.42.3", {"start": v(51.6, 25.73) * mm, "mid": v(51.77, 24.83) * mm, "end": v(52.65, 24.6) * mm});
            skArc(sketch, "E68.43.0", {"start": v(50.18, 20) * mm, "mid": v(50.08, 20.77) * mm, "end": v(49.46, 21.22) * mm});
            skArc(sketch, "E68.43.1", {"start": v(50.61, 22.03) * mm, "mid": v(51.2, 22.72) * mm, "end": v(52.08, 22.48) * mm});
            skArc(sketch, "E68.43.2", {"start": v(50.61, 22.03) * mm, "mid": v(50.21, 21.37) * mm, "end": v(49.46, 21.22) * mm});
            skArc(sketch, "E68.43.3", {"start": v(50.18, 20) * mm, "mid": v(50.44, 19.14) * mm, "end": v(51.34, 19) * mm});
            skArc(sketch, "E68.44.0", {"start": v(49.36, 14.17) * mm, "mid": v(49.19, 14.92) * mm, "end": v(48.52, 15.3) * mm});
            skArc(sketch, "E68.44.1", {"start": v(49.58, 16.23) * mm, "mid": v(50.1, 16.97) * mm, "end": v(51, 16.83) * mm});
            skArc(sketch, "E68.44.2", {"start": v(49.58, 16.23) * mm, "mid": v(49.25, 15.53) * mm, "end": v(48.52, 15.3) * mm});
            skArc(sketch, "E68.44.3", {"start": v(49.36, 14.17) * mm, "mid": v(49.71, 13.33) * mm, "end": v(50.62, 13.29) * mm});
            skArc(sketch, "E68.45.0", {"start": v(49.16, 8.27) * mm, "mid": v(48.91, 9) * mm, "end": v(48.2, 9.3) * mm});
            skArc(sketch, "E68.45.1", {"start": v(49.16, 10.34) * mm, "mid": v(49.6, 11.14) * mm, "end": v(50.5, 11.09) * mm});
            skArc(sketch, "E68.45.2", {"start": v(49.16, 10.34) * mm, "mid": v(48.91, 9.62) * mm, "end": v(48.2, 9.3) * mm});
            skArc(sketch, "E68.45.3", {"start": v(49.16, 8.27) * mm, "mid": v(49.6, 7.48) * mm, "end": v(50.5, 7.53) * mm});
            skArc(sketch, "E68.46.0", {"start": v(49.58, 2.4) * mm, "mid": v(49.25, 3.1) * mm, "end": v(48.52, 3.32) * mm});
            skArc(sketch, "E68.46.1", {"start": v(49.36, 4.45) * mm, "mid": v(49.71, 5.3) * mm, "end": v(50.62, 5.33) * mm});
            skArc(sketch, "E68.46.2", {"start": v(49.36, 4.45) * mm, "mid": v(49.19, 3.7) * mm, "end": v(48.52, 3.32) * mm});
            skArc(sketch, "E68.46.3", {"start": v(49.58, 2.4) * mm, "mid": v(50.1, 1.65) * mm, "end": v(51, 1.8) * mm});
            skArc(sketch, "E68.47.0", {"start": v(50.61, -3.41) * mm, "mid": v(50.21, -2.75) * mm, "end": v(49.46, -2.6) * mm});
            skArc(sketch, "E68.47.1", {"start": v(50.18, -1.39) * mm, "mid": v(50.44, -0.52) * mm, "end": v(51.34, -0.38) * mm});
            skArc(sketch, "E68.47.2", {"start": v(50.18, -1.39) * mm, "mid": v(50.08, -2.15) * mm, "end": v(49.46, -2.6) * mm});
            skArc(sketch, "E68.47.3", {"start": v(50.61, -3.41) * mm, "mid": v(51.2, -4.1) * mm, "end": v(52.08, -3.86) * mm});
            skArc(sketch, "E68.48.0", {"start": v(52.24, -9.08) * mm, "mid": v(51.77, -8.46) * mm, "end": v(51, -8.39) * mm});
            skArc(sketch, "E68.48.1", {"start": v(51.6, -7.1) * mm, "mid": v(51.77, -6.22) * mm, "end": v(52.65, -5.99) * mm});
            skArc(sketch, "E68.48.2", {"start": v(51.6, -7.1) * mm, "mid": v(51.58, -7.88) * mm, "end": v(51, -8.39) * mm});
            skArc(sketch, "E68.48.3", {"start": v(52.24, -9.08) * mm, "mid": v(52.9, -9.7) * mm, "end": v(53.75, -9.37) * mm});
            skArc(sketch, "E68.49.0", {"start": v(54.45, -14.54) * mm, "mid": v(53.93, -13.98) * mm, "end": v(53.16, -13.98) * mm});
            skArc(sketch, "E68.49.1", {"start": v(53.61, -12.65) * mm, "mid": v(53.69, -11.74) * mm, "end": v(54.53, -11.42) * mm});
            skArc(sketch, "E68.49.2", {"start": v(53.61, -12.65) * mm, "mid": v(53.68, -13.42) * mm, "end": v(53.16, -13.98) * mm});
            skArc(sketch, "E68.49.3", {"start": v(54.45, -14.54) * mm, "mid": v(55.18, -15.1) * mm, "end": v(55.98, -14.67) * mm});
            skArc(sketch, "E68.50.0", {"start": v(57.23, -19.74) * mm, "mid": v(56.64, -19.24) * mm, "end": v(55.88, -19.33) * mm});
            skArc(sketch, "E68.50.1", {"start": v(56.2, -17.95) * mm, "mid": v(56.17, -17.04) * mm, "end": v(56.98, -16.64) * mm});
            skArc(sketch, "E68.50.2", {"start": v(56.2, -17.95) * mm, "mid": v(56.34, -18.7) * mm, "end": v(55.88, -19.33) * mm});
            skArc(sketch, "E68.50.3", {"start": v(57.23, -19.74) * mm, "mid": v(58, -20.22) * mm, "end": v(58.76, -19.72) * mm});
            skArc(sketch, "E68.51.0", {"start": v(60.53, -24.63) * mm, "mid": v(59.9, -24.19) * mm, "end": v(59.14, -24.35) * mm});
            skArc(sketch, "E68.51.1", {"start": v(59.31, -22.95) * mm, "mid": v(59.2, -22.05) * mm, "end": v(59.96, -21.56) * mm});
            skArc(sketch, "E68.51.2", {"start": v(59.31, -22.95) * mm, "mid": v(59.53, -23.69) * mm, "end": v(59.14, -24.35) * mm});
            skArc(sketch, "E68.51.3", {"start": v(60.53, -24.63) * mm, "mid": v(61.35, -25.02) * mm, "end": v(62.05, -24.44) * mm});
            skArc(sketch, "E68.52.0", {"start": v(64.32, -29.14) * mm, "mid": v(63.65, -28.77) * mm, "end": v(62.92, -29.01) * mm});
            skArc(sketch, "E68.52.1", {"start": v(62.94, -27.6) * mm, "mid": v(62.73, -26.72) * mm, "end": v(63.43, -26.15) * mm});
            skArc(sketch, "E68.52.2", {"start": v(62.94, -27.6) * mm, "mid": v(63.23, -28.31) * mm, "end": v(62.92, -29.01) * mm});
            skArc(sketch, "E68.52.3", {"start": v(64.32, -29.14) * mm, "mid": v(65.18, -29.44) * mm, "end": v(65.82, -28.8) * mm});
            skArc(sketch, "E68.53.0", {"start": v(68.57, -33.23) * mm, "mid": v(67.86, -32.93) * mm, "end": v(67.15, -33.25) * mm});
            skArc(sketch, "E68.53.1", {"start": v(67.03, -31.85) * mm, "mid": v(66.73, -30.99) * mm, "end": v(67.37, -30.35) * mm});
            skArc(sketch, "E68.53.2", {"start": v(67.03, -31.85) * mm, "mid": v(67.4, -32.52) * mm, "end": v(67.15, -33.25) * mm});
            skArc(sketch, "E68.53.3", {"start": v(68.57, -33.23) * mm, "mid": v(69.45, -33.44) * mm, "end": v(70.02, -32.73) * mm});
            skArc(sketch, "E68.54.0", {"start": v(73.21, -36.86) * mm, "mid": v(72.48, -36.63) * mm, "end": v(71.81, -37.02) * mm});
            skArc(sketch, "E68.54.1", {"start": v(71.54, -35.64) * mm, "mid": v(71.15, -34.82) * mm, "end": v(71.73, -34.12) * mm});
            skArc(sketch, "E68.54.2", {"start": v(71.54, -35.64) * mm, "mid": v(71.98, -36.27) * mm, "end": v(71.81, -37.02) * mm});
            skArc(sketch, "E68.54.3", {"start": v(73.21, -36.86) * mm, "mid": v(74.11, -36.97) * mm, "end": v(74.6, -36.2) * mm});
            skArc(sketch, "E68.55.0", {"start": v(78.22, -39.98) * mm, "mid": v(77.46, -39.83) * mm, "end": v(76.84, -40.29) * mm});
            skArc(sketch, "E68.55.1", {"start": v(76.42, -38.94) * mm, "mid": v(75.95, -38.17) * mm, "end": v(76.45, -37.4) * mm});
            skArc(sketch, "E68.55.2", {"start": v(76.42, -38.94) * mm, "mid": v(76.93, -39.52) * mm, "end": v(76.84, -40.29) * mm});
            skArc(sketch, "E68.55.3", {"start": v(78.22, -39.98) * mm, "mid": v(79.12, -40) * mm, "end": v(79.53, -39.19) * mm});
            skArc(sketch, "E68.56.0", {"start": v(83.52, -42.56) * mm, "mid": v(82.75, -42.5) * mm, "end": v(82.18, -43.01) * mm});
            skArc(sketch, "E68.56.1", {"start": v(81.63, -41.71) * mm, "mid": v(81.08, -41) * mm, "end": v(81.5, -40.19) * mm});
            skArc(sketch, "E68.56.2", {"start": v(81.63, -41.71) * mm, "mid": v(82.19, -42.24) * mm, "end": v(82.18, -43.01) * mm});
            skArc(sketch, "E68.56.3", {"start": v(83.52, -42.56) * mm, "mid": v(84.42, -42.48) * mm, "end": v(84.74, -41.63) * mm});
            skArc(sketch, "E68.57.0", {"start": v(89.06, -44.57) * mm, "mid": v(88.29, -44.58) * mm, "end": v(87.78, -45.16) * mm});
            skArc(sketch, "E68.57.1", {"start": v(87.1, -43.93) * mm, "mid": v(86.47, -43.27) * mm, "end": v(86.8, -42.42) * mm});
            skArc(sketch, "E68.57.2", {"start": v(87.1, -43.93) * mm, "mid": v(87.7, -44.4) * mm, "end": v(87.78, -45.16) * mm});
            skArc(sketch, "E68.57.3", {"start": v(89.06, -44.57) * mm, "mid": v(89.95, -44.4) * mm, "end": v(90.18, -43.52) * mm});
            skArc(sketch, "E68.58.0", {"start": v(94.78, -45.99) * mm, "mid": v(94.02, -46.08) * mm, "end": v(93.57, -46.71) * mm});
            skArc(sketch, "E68.58.1", {"start": v(92.76, -45.56) * mm, "mid": v(92.07, -44.97) * mm, "end": v(92.3, -44.1) * mm});
            skArc(sketch, "E68.58.2", {"start": v(92.76, -45.56) * mm, "mid": v(93.41, -45.96) * mm, "end": v(93.57, -46.71) * mm});
            skArc(sketch, "E68.58.3", {"start": v(94.78, -45.99) * mm, "mid": v(95.65, -45.73) * mm, "end": v(95.79, -44.83) * mm});
            skArc(sketch, "E68.59.0", {"start": v(100.62, -46.8) * mm, "mid": v(99.87, -46.98) * mm, "end": v(99.5, -47.65) * mm});
            skArc(sketch, "E68.59.1", {"start": v(98.56, -46.59) * mm, "mid": v(97.81, -46.07) * mm, "end": v(97.96, -45.17) * mm});
            skArc(sketch, "E68.59.2", {"start": v(98.56, -46.59) * mm, "mid": v(99.26, -46.91) * mm, "end": v(99.5, -47.65) * mm});
            skArc(sketch, "E68.59.3", {"start": v(100.62, -46.8) * mm, "mid": v(101.46, -46.45) * mm, "end": v(101.5, -45.55) * mm});
            skSolve(sketch);
        }
        {
            var Q0;
            Q0=makeQuery(id+"F0.imprint","IMPRINT",FACE,{"disambiguationData":[TD([[makeQuery(id+"F0.imprint","IMPRINT",EDGE,{"derivedFrom":sQuery(id+"F0.wireOp",EDGE,"E2")}),-1.0]])]});
            var Q1;
            Q1=makeQuery(id+"F0.imprint","IMPRINT",FACE,{"disambiguationData":[TD([[makeQuery(id+"F0.imprint","IMPRINT",EDGE,{"derivedFrom":sQuery(id+"F0.wireOp",EDGE,"E1.bottom")}),1.0]])]});
            var Q2;
            Q2=makeQuery(id+"F0.imprint","IMPRINT",FACE,{"disambiguationData":[TD([[makeQuery(id+"F0.imprint","IMPRINT",EDGE,{"derivedFrom":sQuery(id+"F0.wireOp",EDGE,"E68.43.0")}),-1.0]])]});
            var Q3;
            Q3=makeQuery(id+"F0.imprint","IMPRINT",FACE,{"disambiguationData":[TD([[makeQuery(id+"F0.imprint","IMPRINT",EDGE,{"derivedFrom":sQuery(id+"F0.wireOp",EDGE,"E68.2.0")}),-1.0]])]});
            var Q4;
            Q4=makeQuery(id+"F0.imprint","IMPRINT",FACE,{"disambiguationData":[TD([[makeQuery(id+"F0.imprint","IMPRINT",EDGE,{"derivedFrom":sQuery(id+"F0.wireOp",EDGE,"E68.4.0")}),-1.0]])]});
            var Q5;
            Q5=makeQuery(id+"F0.imprint","IMPRINT",FACE,{"disambiguationData":[TD([[makeQuery(id+"F0.imprint","IMPRINT",EDGE,{"derivedFrom":sQuery(id+"F0.wireOp",EDGE,"E68.48.0")}),-1.0]])]});
            var Q6;
            Q6=makeQuery(id+"F0.imprint","IMPRINT",FACE,{"disambiguationData":[TD([[makeQuery(id+"F0.imprint","IMPRINT",EDGE,{"derivedFrom":sQuery(id+"F0.wireOp",EDGE,"E68.33.0")}),-1.0]])]});
            var Q7;
            Q7=makeQuery(id+"F0.imprint","IMPRINT",FACE,{"disambiguationData":[TD([[makeQuery(id+"F0.imprint","IMPRINT",EDGE,{"derivedFrom":sQuery(id+"F0.wireOp",EDGE,"E68.35.0")}),-1.0]])]});
            var Q8;
            Q8=makeQuery(id+"F0.imprint","IMPRINT",FACE,{"disambiguationData":[TD([[makeQuery(id+"F0.imprint","IMPRINT",EDGE,{"derivedFrom":sQuery(id+"F0.wireOp",EDGE,"E68.7.0")}),-1.0]])]});
            var Q9;
            Q9=makeQuery(id+"F0.imprint","IMPRINT",FACE,{"disambiguationData":[TD([[makeQuery(id+"F0.imprint","IMPRINT",EDGE,{"derivedFrom":sQuery(id+"F0.wireOp",EDGE,"E68.51.0")}),-1.0]])]});
            var Q10;
            Q10=makeQuery(id+"F0.imprint","IMPRINT",FACE,{"disambiguationData":[TD([[makeQuery(id+"F0.imprint","IMPRINT",EDGE,{"derivedFrom":sQuery(id+"F0.wireOp",EDGE,"E68.36.0")}),-1.0]])]});
            var Q11;
            Q11=makeQuery(id+"F0.imprint","IMPRINT",FACE,{"disambiguationData":[TD([[makeQuery(id+"F0.imprint","IMPRINT",EDGE,{"derivedFrom":sQuery(id+"F0.wireOp",EDGE,"E68.8.0")}),-1.0]])]});
            var Q12;
            Q12=makeQuery(id+"F0.imprint","IMPRINT",FACE,{"disambiguationData":[TD([[makeQuery(id+"F0.imprint","IMPRINT",EDGE,{"derivedFrom":sQuery(id+"F0.wireOp",EDGE,"E68.52.0")}),-1.0]])]});
            var Q13;
            Q13=makeQuery(id+"F0.imprint","IMPRINT",FACE,{"disambiguationData":[TD([[makeQuery(id+"F0.imprint","IMPRINT",EDGE,{"derivedFrom":sQuery(id+"F0.wireOp",EDGE,"E68.10.0")}),-1.0]])]});
            var Q14;
            Q14=makeQuery(id+"F0.imprint","IMPRINT",FACE,{"disambiguationData":[TD([[makeQuery(id+"F0.imprint","IMPRINT",EDGE,{"derivedFrom":sQuery(id+"F0.wireOp",EDGE,"E68.54.0")}),-1.0]])]});
            var Q15;
            Q15=makeQuery(id+"F0.imprint","IMPRINT",FACE,{"disambiguationData":[TD([[makeQuery(id+"F0.imprint","IMPRINT",EDGE,{"derivedFrom":sQuery(id+"F0.wireOp",EDGE,"E68.38.0")}),-1.0]])]});
            var Q16;
            Q16=makeQuery(id+"F0.imprint","IMPRINT",FACE,{"disambiguationData":[TD([[makeQuery(id+"F0.imprint","IMPRINT",EDGE,{"derivedFrom":sQuery(id+"F0.wireOp",EDGE,"E68.11.0")}),-1.0]])]});
            var Q17;
            Q17=makeQuery(id+"F0.imprint","IMPRINT",FACE,{"disambiguationData":[TD([[makeQuery(id+"F0.imprint","IMPRINT",EDGE,{"derivedFrom":sQuery(id+"F0.wireOp",EDGE,"E68.55.0")}),-1.0]])]});
            var Q18;
            Q18=makeQuery(id+"F0.imprint","IMPRINT",FACE,{"disambiguationData":[TD([[makeQuery(id+"F0.imprint","IMPRINT",EDGE,{"derivedFrom":sQuery(id+"F0.wireOp",EDGE,"E68.39.0")}),-1.0]])]});
            var Q19;
            Q19=makeQuery(id+"F0.imprint","IMPRINT",FACE,{"disambiguationData":[TD([[makeQuery(id+"F0.imprint","IMPRINT",EDGE,{"derivedFrom":sQuery(id+"F0.wireOp",EDGE,"E68.40.0")}),-1.0]])]});
            var Q20;
            Q20=makeQuery(id+"F0.imprint","IMPRINT",FACE,{"disambiguationData":[TD([[makeQuery(id+"F0.imprint","IMPRINT",EDGE,{"derivedFrom":sQuery(id+"F0.wireOp",EDGE,"E68.41.0")}),-1.0]])]});
            var Q21;
            Q21=makeQuery(id+"F0.imprint","IMPRINT",FACE,{"disambiguationData":[TD([[makeQuery(id+"F0.imprint","IMPRINT",EDGE,{"derivedFrom":sQuery(id+"F0.wireOp",EDGE,"E68.14.0")}),-1.0]])]});
            var Q22;
            Q22=makeQuery(id+"F0.imprint","IMPRINT",FACE,{"disambiguationData":[TD([[makeQuery(id+"F0.imprint","IMPRINT",EDGE,{"derivedFrom":sQuery(id+"F0.wireOp",EDGE,"E68.44.0")}),-1.0]])]});
            var Q23;
            Q23=makeQuery(id+"F0.imprint","IMPRINT",FACE,{"disambiguationData":[TD([[makeQuery(id+"F0.imprint","IMPRINT",EDGE,{"derivedFrom":sQuery(id+"F0.wireOp",EDGE,"E68.31.0")}),-1.0]])]});
            var Q24;
            Q24=makeQuery(id+"F0.imprint","IMPRINT",FACE,{"disambiguationData":[TD([[makeQuery(id+"F0.imprint","IMPRINT",EDGE,{"derivedFrom":sQuery(id+"F0.wireOp",EDGE,"E68.29.0")}),-1.0]])]});
            var Q25;
            Q25=makeQuery(id+"F0.imprint","IMPRINT",FACE,{"disambiguationData":[TD([[makeQuery(id+"F0.imprint","IMPRINT",EDGE,{"derivedFrom":sQuery(id+"F0.wireOp",EDGE,"E68.16.0")}),-1.0]])]});
            var Q26;
            Q26=makeQuery(id+"F0.imprint","IMPRINT",FACE,{"disambiguationData":[TD([[makeQuery(id+"F0.imprint","IMPRINT",EDGE,{"derivedFrom":sQuery(id+"F0.wireOp",EDGE,"E68.17.0")}),-1.0]])]});
            var Q27;
            Q27=makeQuery(id+"F0.imprint","IMPRINT",FACE,{"disambiguationData":[TD([[makeQuery(id+"F0.imprint","IMPRINT",EDGE,{"derivedFrom":sQuery(id+"F0.wireOp",EDGE,"E68.21.0")}),-1.0]])]});
            var Q28;
            Q28=makeQuery(id+"F0.imprint","IMPRINT",FACE,{"disambiguationData":[TD([[makeQuery(id+"F0.imprint","IMPRINT",EDGE,{"derivedFrom":sQuery(id+"F0.wireOp",EDGE,"E68.22.0")}),-1.0]])]});
            var Q29;
            Q29=makeQuery(id+"F0.imprint","IMPRINT",FACE,{"disambiguationData":[TD([[makeQuery(id+"F0.imprint","IMPRINT",EDGE,{"derivedFrom":sQuery(id+"F0.wireOp",EDGE,"E68.23.0")}),-1.0]])]});
            var Q30;
            Q30=makeQuery(id+"F0.imprint","IMPRINT",FACE,{"disambiguationData":[TD([[makeQuery(id+"F0.imprint","IMPRINT",EDGE,{"derivedFrom":sQuery(id+"F0.wireOp",EDGE,"E68.24.0")}),-1.0]])]});
            var Q31;
            Q31=makeQuery(id+"F0.imprint","IMPRINT",FACE,{"disambiguationData":[TD([[makeQuery(id+"F0.imprint","IMPRINT",EDGE,{"derivedFrom":sQuery(id+"F0.wireOp",EDGE,"E68.26.0")}),-1.0]])]});
            var Q32;
            Q32=makeQuery(id+"F0.imprint","IMPRINT",FACE,{"disambiguationData":[TD([[makeQuery(id+"F0.imprint","IMPRINT",EDGE,{"derivedFrom":sQuery(id+"F0.wireOp",EDGE,"E68.28.0")}),-1.0]])]});
            var Q33;
            Q33=makeQuery(id+"F0.imprint","IMPRINT",FACE,{"disambiguationData":[TD([[makeQuery(id+"F0.imprint","IMPRINT",EDGE,{"derivedFrom":sQuery(id+"F0.wireOp",EDGE,"E68.3.0")}),-1.0]])]});
            var Q34;
            Q34=makeQuery(id+"F0.imprint","IMPRINT",FACE,{"disambiguationData":[TD([[makeQuery(id+"F0.imprint","IMPRINT",EDGE,{"derivedFrom":sQuery(id+"F0.wireOp",EDGE,"E68.47.0")}),-1.0]])]});
            var Q35;
            Q35=makeQuery(id+"F0.imprint","IMPRINT",FACE,{"disambiguationData":[TD([[makeQuery(id+"F0.imprint","IMPRINT",EDGE,{"derivedFrom":sQuery(id+"F0.wireOp",EDGE,"E68.45.0")}),-1.0]])]});
            var Q36;
            Q36=makeQuery(id+"F0.imprint","IMPRINT",FACE,{"disambiguationData":[TD([[makeQuery(id+"F0.imprint","IMPRINT",EDGE,{"derivedFrom":sQuery(id+"F0.wireOp",EDGE,"E68.1.0")}),-1.0]])]});
            var Q37;
            Q37=makeQuery(id+"F0.imprint","IMPRINT",FACE,{"disambiguationData":[TD([[makeQuery(id+"F0.imprint","IMPRINT",EDGE,{"derivedFrom":sQuery(id+"F0.wireOp",EDGE,"E68.46.0")}),-1.0]])]});
            var Q38;
            Q38=makeQuery(id+"F0.imprint","IMPRINT",FACE,{"disambiguationData":[TD([[makeQuery(id+"F0.imprint","IMPRINT",EDGE,{"derivedFrom":sQuery(id+"F0.wireOp",EDGE,"E68.32.0")}),-1.0]])]});
            var Q39;
            Q39=makeQuery(id+"F0.imprint","IMPRINT",FACE,{"disambiguationData":[TD([[makeQuery(id+"F0.imprint","IMPRINT",EDGE,{"derivedFrom":sQuery(id+"F0.wireOp",EDGE,"E68.5.0")}),-1.0]])]});
            var Q40;
            Q40=makeQuery(id+"F0.imprint","IMPRINT",FACE,{"disambiguationData":[TD([[makeQuery(id+"F0.imprint","IMPRINT",EDGE,{"derivedFrom":sQuery(id+"F0.wireOp",EDGE,"E68.49.0")}),-1.0]])]});
            var Q41;
            Q41=makeQuery(id+"F0.imprint","IMPRINT",FACE,{"disambiguationData":[TD([[makeQuery(id+"F0.imprint","IMPRINT",EDGE,{"derivedFrom":sQuery(id+"F0.wireOp",EDGE,"E68.34.0")}),-1.0]])]});
            var Q42;
            Q42=makeQuery(id+"F0.imprint","IMPRINT",FACE,{"disambiguationData":[TD([[makeQuery(id+"F0.imprint","IMPRINT",EDGE,{"derivedFrom":sQuery(id+"F0.wireOp",EDGE,"E68.6.0")}),-1.0]])]});
            var Q43;
            Q43=makeQuery(id+"F0.imprint","IMPRINT",FACE,{"disambiguationData":[TD([[makeQuery(id+"F0.imprint","IMPRINT",EDGE,{"derivedFrom":sQuery(id+"F0.wireOp",EDGE,"E68.50.0")}),-1.0]])]});
            var Q44;
            Q44=makeQuery(id+"F0.imprint","IMPRINT",FACE,{"disambiguationData":[TD([[makeQuery(id+"F0.imprint","IMPRINT",EDGE,{"derivedFrom":sQuery(id+"F0.wireOp",EDGE,"E68.37.0")}),-1.0]])]});
            var Q45;
            Q45=makeQuery(id+"F0.imprint","IMPRINT",FACE,{"disambiguationData":[TD([[makeQuery(id+"F0.imprint","IMPRINT",EDGE,{"derivedFrom":sQuery(id+"F0.wireOp",EDGE,"E68.9.0")}),-1.0]])]});
            var Q46;
            Q46=makeQuery(id+"F0.imprint","IMPRINT",FACE,{"disambiguationData":[TD([[makeQuery(id+"F0.imprint","IMPRINT",EDGE,{"derivedFrom":sQuery(id+"F0.wireOp",EDGE,"E68.53.0")}),-1.0]])]});
            var Q47;
            Q47=makeQuery(id+"F0.imprint","IMPRINT",FACE,{"disambiguationData":[TD([[makeQuery(id+"F0.imprint","IMPRINT",EDGE,{"derivedFrom":sQuery(id+"F0.wireOp",EDGE,"E68.12.0")}),-1.0]])]});
            var Q48;
            Q48=makeQuery(id+"F0.imprint","IMPRINT",FACE,{"disambiguationData":[TD([[makeQuery(id+"F0.imprint","IMPRINT",EDGE,{"derivedFrom":sQuery(id+"F0.wireOp",EDGE,"E68.56.0")}),-1.0]])]});
            var Q49;
            Q49=makeQuery(id+"F0.imprint","IMPRINT",FACE,{"disambiguationData":[TD([[makeQuery(id+"F0.imprint","IMPRINT",EDGE,{"derivedFrom":sQuery(id+"F0.wireOp",EDGE,"E68.13.0")}),-1.0]])]});
            var Q50;
            Q50=makeQuery(id+"F0.imprint","IMPRINT",FACE,{"disambiguationData":[TD([[makeQuery(id+"F0.imprint","IMPRINT",EDGE,{"derivedFrom":sQuery(id+"F0.wireOp",EDGE,"E68.57.0")}),-1.0]])]});
            var Q51;
            Q51=makeQuery(id+"F0.imprint","IMPRINT",FACE,{"disambiguationData":[TD([[makeQuery(id+"F0.imprint","IMPRINT",EDGE,{"derivedFrom":sQuery(id+"F0.wireOp",EDGE,"E68.58.0")}),-1.0]])]});
            var Q52;
            Q52=makeQuery(id+"F0.imprint","IMPRINT",FACE,{"disambiguationData":[TD([[makeQuery(id+"F0.imprint","IMPRINT",EDGE,{"derivedFrom":sQuery(id+"F0.wireOp",EDGE,"E68.42.0")}),-1.0]])]});
            var Q53;
            Q53=makeQuery(id+"F0.imprint","IMPRINT",FACE,{"disambiguationData":[TD([[makeQuery(id+"F0.imprint","IMPRINT",EDGE,{"derivedFrom":sQuery(id+"F0.wireOp",EDGE,"E68.15.0")}),-1.0]])]});
            var Q54;
            Q54=makeQuery(id+"F0.imprint","IMPRINT",FACE,{"disambiguationData":[TD([[makeQuery(id+"F0.imprint","IMPRINT",EDGE,{"derivedFrom":sQuery(id+"F0.wireOp",EDGE,"E68.59.0")}),-1.0]])]});
            var Q55;
            Q55=makeQuery(id+"F0.imprint","IMPRINT",FACE,{"disambiguationData":[TD([[makeQuery(id+"F0.imprint","IMPRINT",EDGE,{"derivedFrom":sQuery(id+"F0.wireOp",EDGE,"E64")}),-1.0]])]});
            var Q56;
            Q56=makeQuery(id+"F0.imprint","IMPRINT",FACE,{"disambiguationData":[TD([[makeQuery(id+"F0.imprint","IMPRINT",EDGE,{"derivedFrom":sQuery(id+"F0.wireOp",EDGE,"E68.30.0")}),-1.0]])]});
            var Q57;
            Q57=makeQuery(id+"F0.imprint","IMPRINT",FACE,{"disambiguationData":[TD([[makeQuery(id+"F0.imprint","IMPRINT",EDGE,{"derivedFrom":sQuery(id+"F0.wireOp",EDGE,"E68.18.0")}),-1.0]])]});
            var Q58;
            Q58=makeQuery(id+"F0.imprint","IMPRINT",FACE,{"disambiguationData":[TD([[makeQuery(id+"F0.imprint","IMPRINT",EDGE,{"derivedFrom":sQuery(id+"F0.wireOp",EDGE,"E68.19.0")}),-1.0]])]});
            var Q59;
            Q59=makeQuery(id+"F0.imprint","IMPRINT",FACE,{"disambiguationData":[TD([[makeQuery(id+"F0.imprint","IMPRINT",EDGE,{"derivedFrom":sQuery(id+"F0.wireOp",EDGE,"E68.20.0")}),-1.0]])]});
            var Q60;
            Q60=makeQuery(id+"F0.imprint","IMPRINT",FACE,{"disambiguationData":[TD([[makeQuery(id+"F0.imprint","IMPRINT",EDGE,{"derivedFrom":sQuery(id+"F0.wireOp",EDGE,"E68.25.0")}),-1.0]])]});
            var Q61;
            Q61=makeQuery(id+"F0.imprint","IMPRINT",FACE,{"disambiguationData":[TD([[makeQuery(id+"F0.imprint","IMPRINT",EDGE,{"derivedFrom":sQuery(id+"F0.wireOp",EDGE,"E68.27.0")}),-1.0]])]});
            extrude(context, id + "F1", {"entities" : qUnion([Q0, Q1, Q2, Q3, Q4, Q5, Q6, Q7, Q8, Q9, Q10, Q11, Q12, Q13, Q14, Q15, Q16, Q17, Q18, Q19, Q20, Q21, Q22, Q23, Q24, Q25, Q26, Q27, Q28, Q29, Q30, Q31, Q32, Q33, Q34, Q35, Q36, Q37, Q38, Q39, Q40, Q41, Q42, Q43, Q44, Q45, Q46, Q47, Q48, Q49, Q50, Q51, Q52, Q53, Q54, Q55, Q56, Q57, Q58, Q59, Q60, Q61]), "depth" : 4 * mm});
        }
        {
            var Q0;
            Q0=makeQuery(id+"F0.imprint","IMPRINT",FACE,{"disambiguationData":[TD([[makeQuery(id+"F0.imprint","IMPRINT",EDGE,{"derivedFrom":sQuery(id+"F0.wireOp",EDGE,"E55")}),-1.0]])]});
            extrude(context, id + "F2", {"entities" : qUnion([Q0]), "depth" : 80 * mm});
        }
    });
